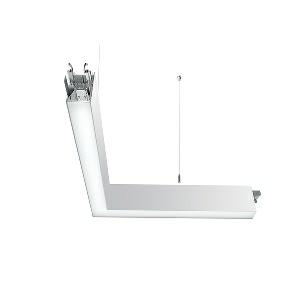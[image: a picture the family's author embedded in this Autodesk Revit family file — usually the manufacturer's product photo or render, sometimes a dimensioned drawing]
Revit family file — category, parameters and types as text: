
# Revit family: dotoo_line_-_dlp_1500_840_d_lr_mid_00807693_d79e
name_source: partatom
category: Lighting Fixtures
units: mm (PartAtom-declared; Revit-internal decimal feet)

## family parameters
Cut with Voids When Loaded = No
Host = Face
Light Source = No
Part Type = Normal
Room Calculation Point = No
Round Connector Dimension = Use Diameter
Shared = No

## types (1)
- DOTOO.line - DLP 1500/840/D/LR MID (1 x LED, 1350 lm, 4000K)
    Apparent Load = 13 VA
    Approval mark = CE
    CIE Flux Codes = 67 91 98 100 100
    Color Rendering = 80-89
    Color Temperature = 4000K
    Control Gear = Electronic ballast
    Default Elevation = 1800 mm
    Description = DLP 1500/840/D|Suspended luminaire|light source: LED|connected load: 220-240 V, 50/60 Hz|Power consumption: approx. 13 W|standby: approx. 0,20|luminous flux: 1350 lm|luminous efficacy: 103 lm/W|light distribution: Direct|direct ratio: approx. 100 %|colour temperature: Cold white, ca. 4000 K|color rendering index (CRI): >= 80|chromaticity tolerance:  3 SDCM|System of protection: IP 40|technology: Continuously dimmable|luminaire body|material: Sectional aluminium|colour: White|lamp cover: Acrylic (PMMA), Clear|Fastening: Steel cable 0.3 - 0.7 m|glare control: Prism aperture|luminance(L65): <= 3000 cd/m|unified glare rating(4H 8H): <=  19|special features: DALI Load 1x, TouchDIM - dimming via standard switch, Through-wired, up to 18 m on one mains connection, Flicker-free, Continous light without dark z, Suitable as emergency lighting, 90░ rerouting on the right sid, Mechanical and electrical connection of the individual modules without tools|
    Frequency = 50 Hz
    Height = 110 mm
    Lamp = 1 x LED
    Lamp Light Flux = 1350 lm
    Lamp count = 1
    Length = 600 mm
    Luminous efficacy = 104 lm/W
    Manufacturer = Waldmann
    ModVariant = No
    Model = 00807693
    Mounting Place = Ceiling
    Mounting Type = Pendant
    Number of Poles = 1
    OnlyDefault = Yes
    Power Factor = 1
    Product Name = DOTOO.line - DLP 1500/840/D/LR MID
    Product group = Suspended luminaire
    ProductGroupID = 9
    Protection Class = Protection class I
    Protection Degree = IP 40
    RLX_Detail_Level = 1
    RLX_Emergency_Light_Flux = 0 lm
    RLX_Emergency_Type = 0
    RLX_Emergency_Type_DB = No
    RlxData = <blob elided: 21193 chars, md5=9fac2c43>
    Socket = socket
    Standby Power = 0 W
    System Light Flux = 1350 lm
    System Power = 13 W
    Type Comments = Product without accessories
    Type Image = ilp_dlp_lr_ws.jpg
    URL = http://relux.com
    VarID = ---
    Voltage = 230 V
    Voltage Range = 220-240 V
    Weight = 0.00 kg
    Width = 600 mm

## geometry (parser evidence)
native form markers: Blend x4, Sweep x10
no freeform markers — native parametric forms only
